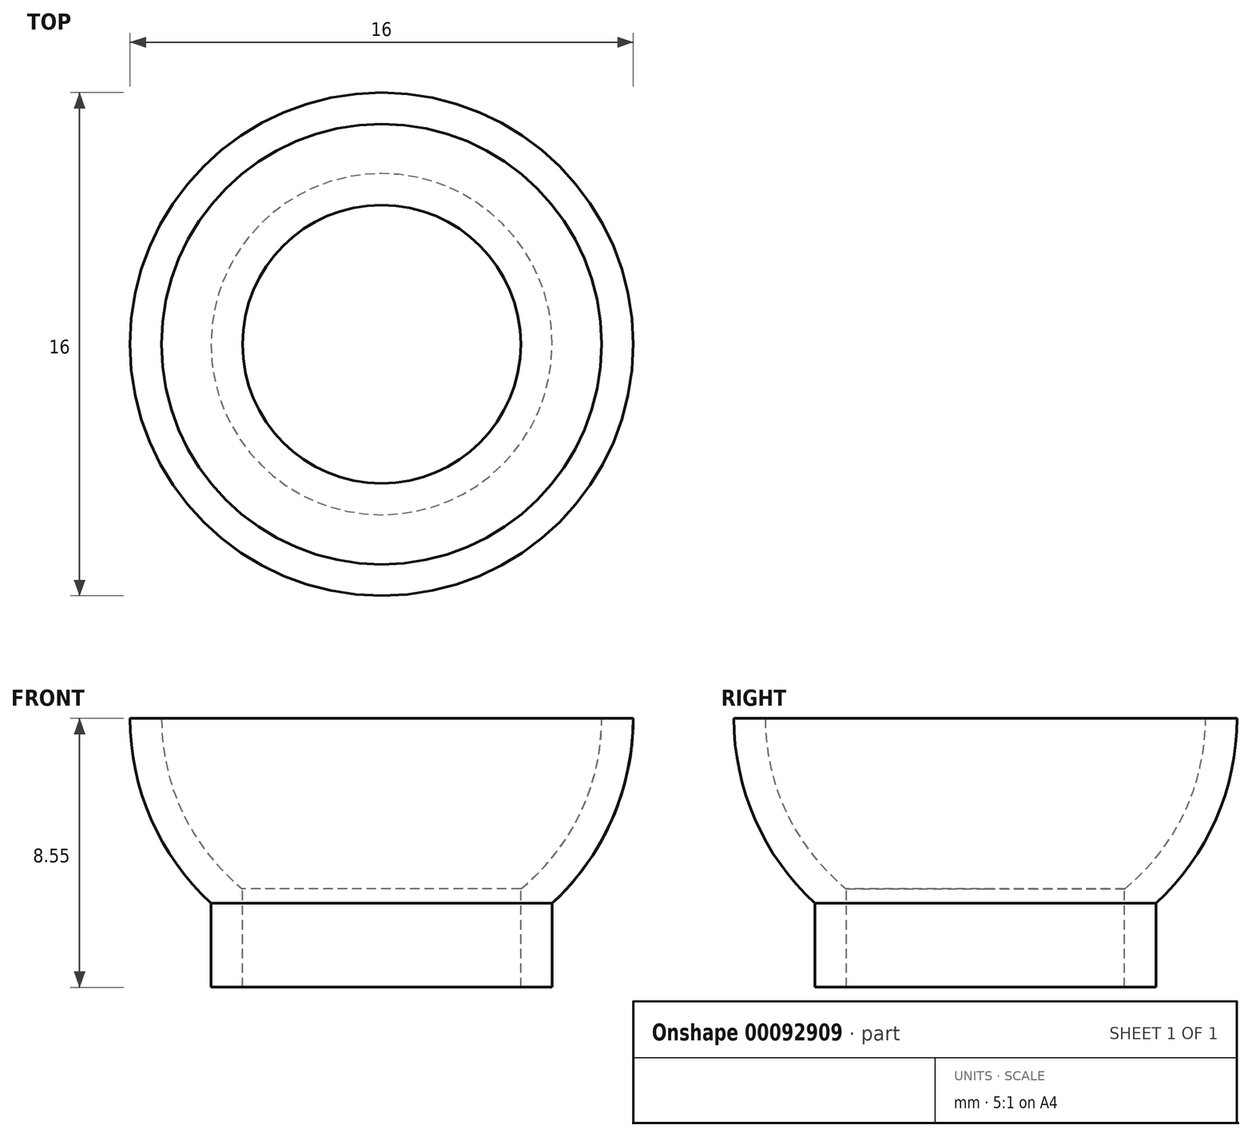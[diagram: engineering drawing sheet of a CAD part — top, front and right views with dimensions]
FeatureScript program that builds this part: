
annotation { "Feature Type Name" : "Feature", "Feature Type Description" : "" }
export const myFeature = defineFeature(function(context is Context, id is Id, definition is map)
    precondition{}
    {
        {
            var Q0;
            Q0=qCreatedBy(makeId("Front.planeOp"),FACE);
            var sketch = newSketch(context, id + "F0", { "sketchPlane" : qUnion([Q0])});
            skArc(sketch, "E0", {"start": v(8, 0) * mm, "mid": v(5.66, -5.66) * mm, "end": v(0, -8) * mm});
            skLineSegment(sketch, "E1", {"start": v(0, 0) * mm, "end": v(0, -8.55) * mm});
            skLineSegment(sketch, "E2", {"start": v(0, -8.55) * mm, "end": v(5.42, -8.55) * mm});
            skLineSegment(sketch, "E3", {"start": v(5.42, -8.55) * mm, "end": v(5.42, -5.88) * mm});
            skLineSegment(sketch, "E4", {"start": v(0, 0) * mm, "end": v(8, 0) * mm});
            skSolve(sketch);
        }
        {
            var Q0;
            Q0 = qSketchRegion(id + "F0", true);
            var Q1;
            Q1=sQuery(id+"F0.wireOp",EDGE,"E1");
            revolve(context, id + "F1", {"entities" : qUnion([Q0]), "axis" : qUnion([Q1]), "revolveType" : RevolveType.FULL});
        }
        {
            var Q0;
            Q0=makeQuery(id+"F1.opRevolve","SWEPT_FACE",FACE,{"disambiguationData":[OSD([sQuery(id+"F0.wireOp",EDGE,"E4")])]});
            var Q1;
            Q1=makeQuery(id+"F1.opRevolve","SWEPT_FACE",FACE,{"disambiguationData":[OSD([sQuery(id+"F0.wireOp",EDGE,"E2")])]});
            shell(context, id + "F2", {"entities" : qUnion([Q0, Q1]), "thickness" : 1 * mm});
        }
    });
